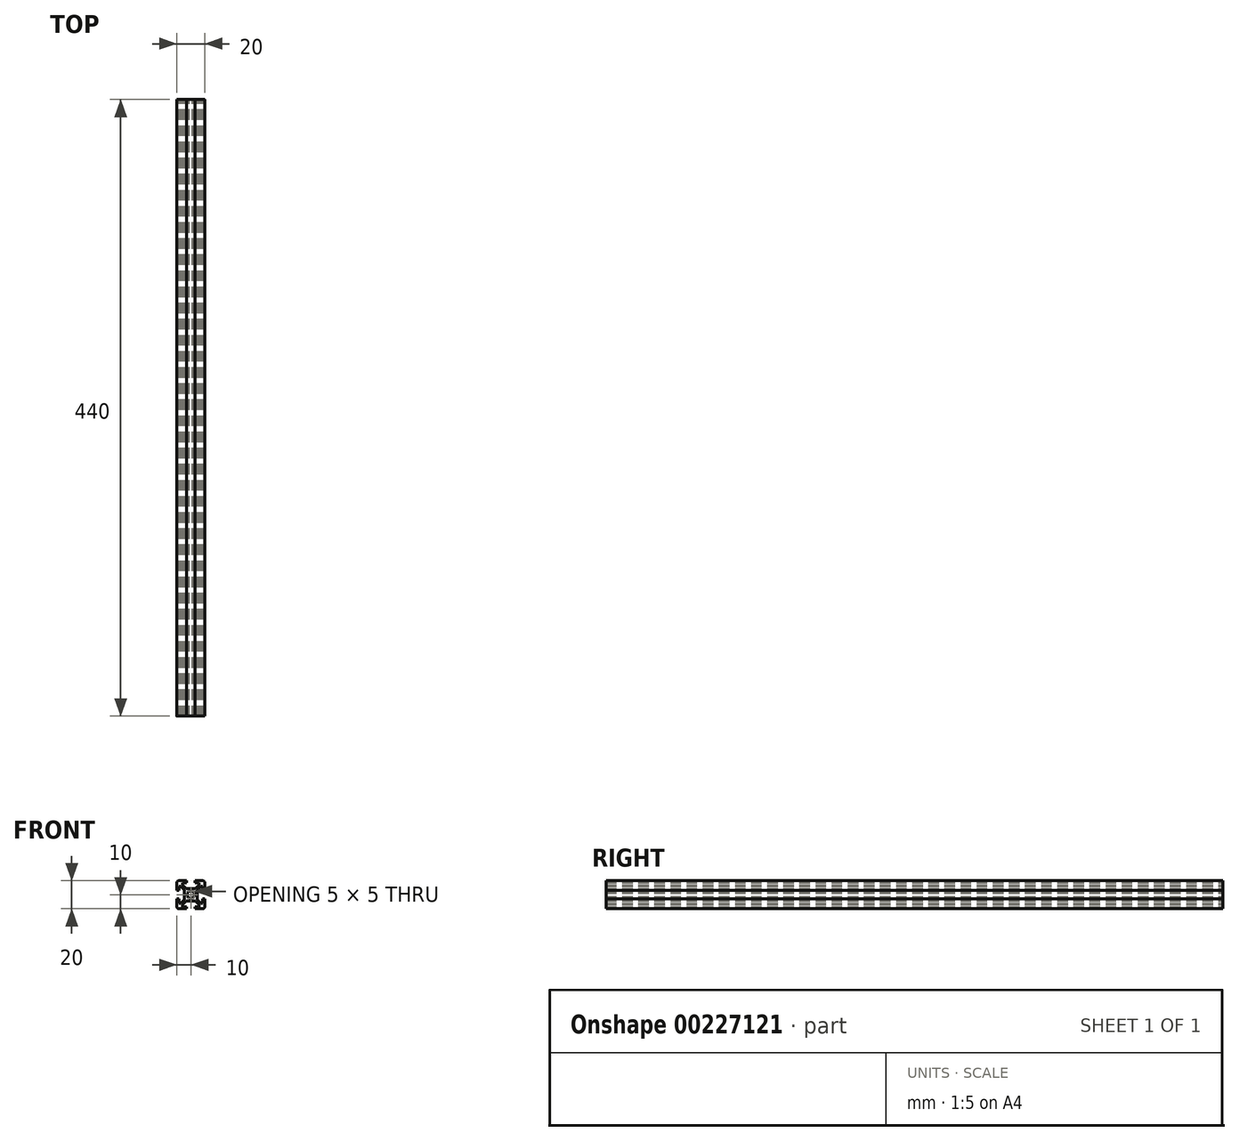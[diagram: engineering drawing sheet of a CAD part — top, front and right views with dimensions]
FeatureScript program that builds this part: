
annotation { "Feature Type Name" : "Feature", "Feature Type Description" : "" }
export const myFeature = defineFeature(function(context is Context, id is Id, definition is map)
    precondition{}
    {
        {
            var Q0;
            Q0=qCreatedBy(makeId("Front.planeOp"),FACE);
            var sketch = newSketch(context, id + "F0", { "sketchPlane" : qUnion([Q0])});
            skLineSegment(sketch, "E0.bottom", {"start": v(8.5, -10) * mm, "end": v(3, -10) * mm});
            skLineSegment(sketch, "E0.top", {"start": v(8.5, 10) * mm, "end": v(3, 10) * mm});
            skLineSegment(sketch, "E0.left", {"start": v(10, -8.5) * mm, "end": v(10, -3) * mm});
            skLineSegment(sketch, "E0.right", {"start": v(-10, -8.5) * mm, "end": v(-10, -3) * mm});
            skPoint(sketch, "E0.middle", {"position": v(0, 0) * mm});
            skLineSegment(sketch, "E1.bottom", {"start": v(6, -8.5) * mm, "end": v(3, -8.5) * mm});
            skLineSegment(sketch, "E1.top", {"start": v(6, 8.5) * mm, "end": v(3, 8.5) * mm});
            skLineSegment(sketch, "E1.left", {"start": v(8.5, -6) * mm, "end": v(8.5, -3) * mm});
            skLineSegment(sketch, "E1.right", {"start": v(-8.5, -6) * mm, "end": v(-8.5, -3) * mm});
            skLineSegment(sketch, "E2.bottom", {"start": v(3.44, -4.5) * mm, "end": v(-3.44, -4.5) * mm});
            skLineSegment(sketch, "E2.top", {"start": v(3.44, 4.5) * mm, "end": v(-3.44, 4.5) * mm});
            skLineSegment(sketch, "E2.left", {"start": v(4.5, -3.44) * mm, "end": v(4.5, 3.44) * mm});
            skLineSegment(sketch, "E2.right", {"start": v(-4.5, -3.44) * mm, "end": v(-4.5, 3.44) * mm});
            skLineSegment(sketch, "E3.bottom", {"start": v(8.5, -6) * mm, "end": v(7.06, -6) * mm});
            skLineSegment(sketch, "E3.top", {"start": v(8.5, 6) * mm, "end": v(7.06, 6) * mm});
            skLineSegment(sketch, "E4.left", {"start": v(6, -8.5) * mm, "end": v(6, -7.06) * mm});
            skLineSegment(sketch, "E4.right", {"start": v(-6, -8.5) * mm, "end": v(-6, -7.06) * mm});
            skPoint(sketch, "E5.orphan", {"position": v(-8.5, 8.5) * mm});
            skPoint(sketch, "E6.orphan", {"position": v(8.5, 8.5) * mm});
            skPoint(sketch, "E7.orphan", {"position": v(8.5, -8.5) * mm});
            skPoint(sketch, "E8.orphan", {"position": v(-8.5, -8.5) * mm});
            skLineSegment(sketch, "E9.trimOffspring", {"start": v(-6, 7.06) * mm, "end": v(-6, 8.5) * mm});
            skLineSegment(sketch, "E10.trimOffspring", {"start": v(-7.06, 6) * mm, "end": v(-8.5, 6) * mm});
            skLineSegment(sketch, "E11.trimOffspring", {"start": v(6, 7.06) * mm, "end": v(6, 8.5) * mm});
            skLineSegment(sketch, "E12.trimOffspring", {"start": v(-7.06, -6) * mm, "end": v(-8.5, -6) * mm});
            skLineSegment(sketch, "E13", {"start": v(-10, 10) * mm, "end": v(0, 0) * mm, "construction": true});
            skLineSegment(sketch, "E14", {"start": v(10, 10) * mm, "end": v(0, 0) * mm, "construction": true});
            skLineSegment(sketch, "E15", {"start": v(-6, 7.06) * mm, "end": v(-3.44, 4.5) * mm});
            skPoint(sketch, "E15.endSnap0", {"position": v(7.25, -6) * mm});
            skLineSegment(sketch, "E16", {"start": v(6, -7.06) * mm, "end": v(3.44, -4.5) * mm});
            skLineSegment(sketch, "E17", {"start": v(7.06, 6) * mm, "end": v(4.5, 3.44) * mm});
            skLineSegment(sketch, "E18", {"start": v(6, 7.06) * mm, "end": v(3.44, 4.5) * mm});
            skPoint(sketch, "E19.orphan", {"position": v(6, -6) * mm});
            skPoint(sketch, "E20.orphan", {"position": v(-4.5, -4.5) * mm});
            skPoint(sketch, "E21.orphan", {"position": v(-4.5, 4.5) * mm});
            skPoint(sketch, "E22.orphan", {"position": v(4.5, 4.5) * mm});
            skPoint(sketch, "E23.orphan", {"position": v(4.5, -4.5) * mm});
            skLineSegment(sketch, "E24.trimOffspring", {"start": v(4.5, -3.44) * mm, "end": v(7.06, -6) * mm});
            skLineSegment(sketch, "E25.trimOffspring", {"start": v(-3.44, -4.5) * mm, "end": v(-6, -7.06) * mm});
            skLineSegment(sketch, "E26.trimOffspring", {"start": v(-4.5, -3.44) * mm, "end": v(-7.06, -6) * mm});
            skLineSegment(sketch, "E27.trimOffspring", {"start": v(-4.5, 3.44) * mm, "end": v(-7.06, 6) * mm});
            skLineSegment(sketch, "E28.bottom", {"start": v(8.5, -3) * mm, "end": v(10, -3) * mm});
            skLineSegment(sketch, "E28.top", {"start": v(8.5, 3) * mm, "end": v(10, 3) * mm});
            skPoint(sketch, "E28.middle", {"position": v(10, 0) * mm});
            skLineSegment(sketch, "E29.left", {"start": v(3, 8.5) * mm, "end": v(3, 10) * mm});
            skLineSegment(sketch, "E29.right", {"start": v(-3, 8.5) * mm, "end": v(-3, 10) * mm});
            skPoint(sketch, "E29.middle", {"position": v(0, 10) * mm});
            skLineSegment(sketch, "E30.bottom", {"start": v(-8.5, 3) * mm, "end": v(-10, 3) * mm});
            skLineSegment(sketch, "E30.top", {"start": v(-8.5, -3) * mm, "end": v(-10, -3) * mm});
            skPoint(sketch, "E30.middle", {"position": v(-10, 0) * mm});
            skLineSegment(sketch, "E31.left", {"start": v(3, -8.5) * mm, "end": v(3, -10) * mm});
            skLineSegment(sketch, "E31.right", {"start": v(-3, -8.5) * mm, "end": v(-3, -10) * mm});
            skPoint(sketch, "E31.middle", {"position": v(0, -10) * mm});
            skPoint(sketch, "E32.orphan", {"position": v(3, 11.5) * mm});
            skPoint(sketch, "E33.orphan", {"position": v(-3, 11.5) * mm});
            skLineSegment(sketch, "E34.trimOffspring", {"start": v(-3, 10) * mm, "end": v(-8.5, 10) * mm});
            skLineSegment(sketch, "E35.trimOffspring", {"start": v(-3, 8.5) * mm, "end": v(-6, 8.5) * mm});
            skPoint(sketch, "E28.right.end.orphan", {"position": v(11.5, 3) * mm});
            skPoint(sketch, "E36.orphan", {"position": v(11.5, -3) * mm});
            skLineSegment(sketch, "E37.trimOffspring", {"start": v(10, 3) * mm, "end": v(10, 8.5) * mm});
            skLineSegment(sketch, "E38.trimOffspring", {"start": v(8.5, 3) * mm, "end": v(8.5, 6) * mm});
            skPoint(sketch, "E39.orphan", {"position": v(3, -11.5) * mm});
            skPoint(sketch, "E40.orphan", {"position": v(-3, -11.5) * mm});
            skLineSegment(sketch, "E41.trimOffspring", {"start": v(-3, -10) * mm, "end": v(-8.5, -10) * mm});
            skLineSegment(sketch, "E42.trimOffspring", {"start": v(-3, -8.5) * mm, "end": v(-6, -8.5) * mm});
            skPoint(sketch, "E30.right.end.orphan", {"position": v(-11.5, -3) * mm});
            skPoint(sketch, "E43.orphan", {"position": v(-11.5, 3) * mm});
            skLineSegment(sketch, "E44.trimOffspring", {"start": v(-10, 3) * mm, "end": v(-10, 8.5) * mm});
            skLineSegment(sketch, "E45.trimOffspring", {"start": v(-8.5, 3) * mm, "end": v(-8.5, 6) * mm});
            skLineSegment(sketch, "E46.trimOffspring", {"start": v(0, 0) * mm, "end": v(10, -10) * mm, "construction": true});
            skLineSegment(sketch, "E47.trimOffspring", {"start": v(0, 0) * mm, "end": v(-10, -10) * mm, "construction": true});
            skArc(sketch, "E48", {"start": v(1.16, 2.22) * mm, "mid": v(0, 2.5) * mm, "end": v(-1.16, 2.22) * mm});
            skLineSegment(sketch, "E49", {"start": v(-2.5, -1.44) * mm, "end": v(1.44, 2.5) * mm});
            skLineSegment(sketch, "E50", {"start": v(2.5, 1.44) * mm, "end": v(-1.44, -2.5) * mm});
            skLineSegment(sketch, "E51", {"start": v(1.44, -2.5) * mm, "end": v(-2.5, 1.44) * mm});
            skLineSegment(sketch, "E52", {"start": v(-1.44, 2.5) * mm, "end": v(2.5, -1.44) * mm});
            skLineSegment(sketch, "E53", {"start": v(2.5, 1.44) * mm, "end": v(2.5, -1.44) * mm, "construction": true});
            skLineSegment(sketch, "E54", {"start": v(1.44, -2.5) * mm, "end": v(-1.44, -2.5) * mm, "construction": true});
            skLineSegment(sketch, "E55", {"start": v(-2.5, -1.44) * mm, "end": v(-2.5, 1.44) * mm, "construction": true});
            skLineSegment(sketch, "E56", {"start": v(-1.44, 2.5) * mm, "end": v(1.44, 2.5) * mm, "construction": true});
            skLineSegment(sketch, "E57", {"start": v(-1.44, 2.5) * mm, "end": v(-2.5, 1.44) * mm});
            skLineSegment(sketch, "E58", {"start": v(1.44, 2.5) * mm, "end": v(2.5, 1.44) * mm});
            skLineSegment(sketch, "E59", {"start": v(2.5, -1.44) * mm, "end": v(1.44, -2.5) * mm});
            skLineSegment(sketch, "E60", {"start": v(-1.44, -2.5) * mm, "end": v(-2.5, -1.44) * mm});
            skArc(sketch, "E61.trimOffspring", {"start": v(-2.22, 1.16) * mm, "mid": v(-2.5, 0) * mm, "end": v(-2.22, -1.16) * mm});
            skArc(sketch, "E62.trimOffspring", {"start": v(-1.16, -2.22) * mm, "mid": v(0, -2.5) * mm, "end": v(1.16, -2.22) * mm});
            skArc(sketch, "E63.trimOffspring", {"start": v(2.22, -1.16) * mm, "mid": v(2.5, 0) * mm, "end": v(2.22, 1.16) * mm});
            skPoint(sketch, "E64.visualSharp", {"position": v(10, 10) * mm});
            skArc(sketch, "E64.filletArc", {"start": v(10, 8.5) * mm, "mid": v(9.56, 9.56) * mm, "end": v(8.5, 10) * mm});
            skPoint(sketch, "E65.visualSharp", {"position": v(10, -10) * mm});
            skArc(sketch, "E65.filletArc", {"start": v(8.5, -10) * mm, "mid": v(9.56, -9.56) * mm, "end": v(10, -8.5) * mm});
            skPoint(sketch, "E66.visualSharp", {"position": v(-10, -10) * mm});
            skArc(sketch, "E66.filletArc", {"start": v(-10, -8.5) * mm, "mid": v(-9.56, -9.56) * mm, "end": v(-8.5, -10) * mm});
            skPoint(sketch, "E67.visualSharp", {"position": v(-10, 10) * mm});
            skArc(sketch, "E67.filletArc", {"start": v(-8.5, 10) * mm, "mid": v(-9.56, 9.56) * mm, "end": v(-10, 8.5) * mm});
            skSolve(sketch);
        }
        {
            assignVariable(context, id + "F2", {"name" : "Length", "anyValue" : 440});
        }
        {
            var Q0;
            Q0=qSketchRegion(id+"F0",true);
            extrude(context, id + "F1", {"entities" : qUnion([Q0]), "depth" : (getVariable(context, 'Length')) * mm});
        }
    });
